# Revit family: DC_Holyoake_OutsideLouver_OHL-C-102_supply_12
name_source: partatom
category: Air Terminals
revit_build: Autodesk Revit 2013 (Build: 20120221_2030(x64)
units: mm (PartAtom-declared; Revit-internal decimal feet)

## types (1)
- OHL-C-102
    Accessories = Aluminium Bird mesh or insect mesh (fibreglass)
    Blade Array Count = 7.541176
    Blade Count = 7
    Blade Cut Setout = 714 mm
    Blade Height = 134.9 mm  [stored 0.442585 ft]
    Blade Length = 684.2 mm  [stored 2.24475 ft]
    Blade Offset = 0.9 mm  [stored 0.00295276 ft]
    Blade Pitch = 102 mm
    Blade Width = 101.4 mm  [stored 0.332677 ft]
    Channel Thickness = 103.2 mm  [stored 0.338583 ft]
    Channel Width = 25.4 mm  [stored 0.0833333 ft]
    Connector Height = 745.2 mm
    Connector Width = 660.2 mm
    Description = Weather Louvres shall be Holyoake Model OHL-C-102 curved profile 102mm louvred blades set at 102mm centres and constructed in a channel (C) frame to suit the installation profile.  Weather Louvres shall be of extruded aluminium construction and finished in natural anodised or powdercoat and fitted with accessories and dampers where indicated as manufactured by Holyoake.
    Exact Neck Height = 820 mm  [stored 2.69029 ft]
    Exact Neck Width = 735 mm  [stored 2.41142 ft]
    Holyoake Product Range = Outside Louvres
    Manufacturer = Holyoake
    Material - Body = Holyoake Aluminium
    Material - Face = Holyoake Aluminium
    Max Flow = 2000.0 L/s
    Min Flow = 100.0 L/s
    Model = OHL-C-102
    Noise Level NC Max = 0.00 NC
    Noise Level NC Min = 0.00 NC
    Nominal Height = 826 mm  [stored 2.70997 ft]
    Nominal Width = 741 mm  [stored 2.4311 ft]
    Overall Depth = 38.3 mm
    Overall Opening = 769.2 mm  [stored 2.52362 ft]
    Static Pressure Max = 0.0 Pa
    Static Pressure Min = 0.0 Pa
    Top Blade Height = 55.2 mm
    Type Comments = 102mm Horizontal Curved Profile Louvers in Channel Surround
    URL = http://www.holyoake.com

note: [stored X ft] marks values corroborated as IEEE doubles in the binary element streams (Revit-internal decimal feet)

## geometry (parser evidence)
native form markers: Blend x6, Sweep x6
no freeform markers — native parametric forms only
